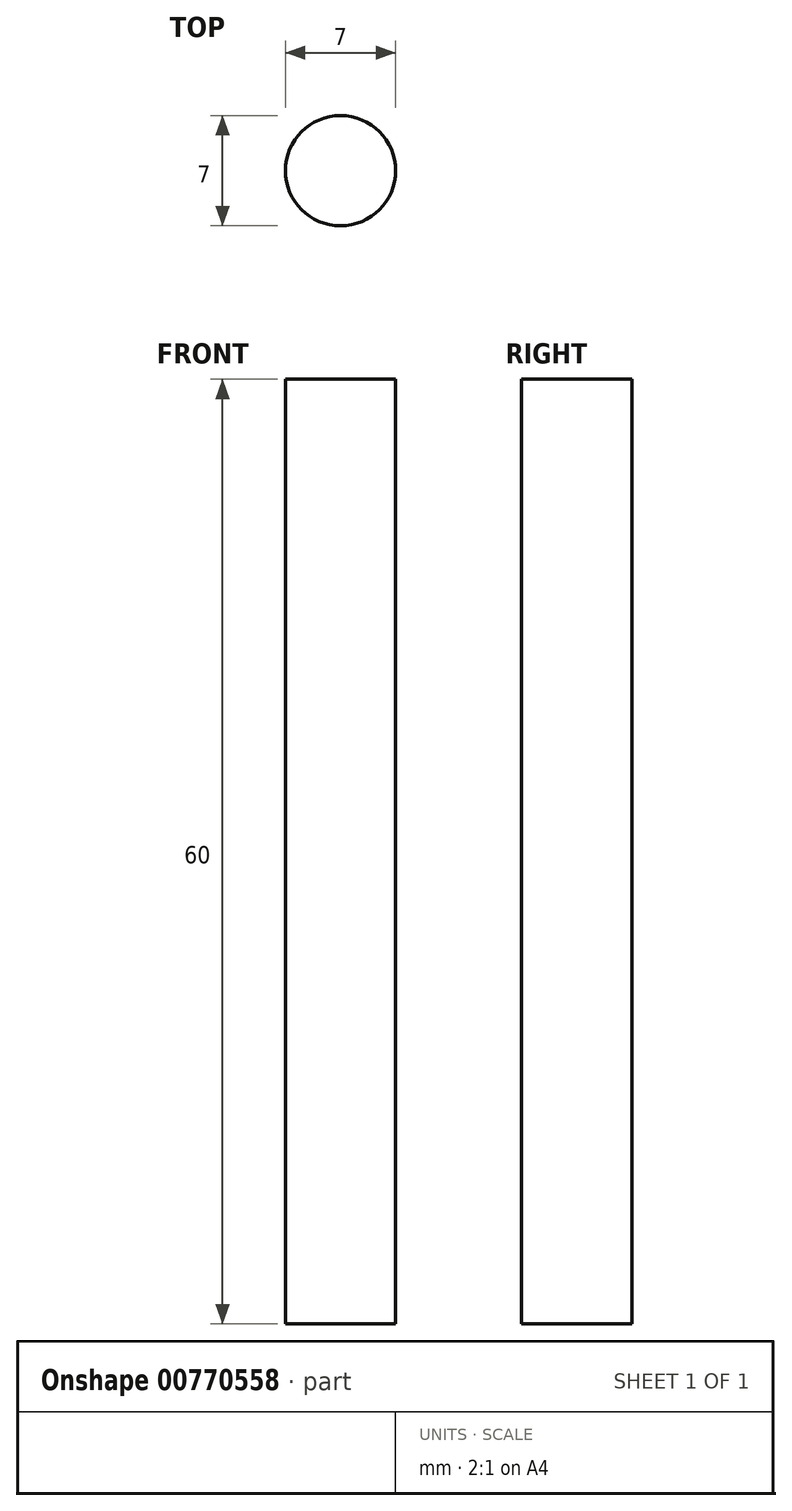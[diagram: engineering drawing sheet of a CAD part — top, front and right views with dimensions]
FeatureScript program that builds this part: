
annotation { "Feature Type Name" : "Feature", "Feature Type Description" : "" }
export const myFeature = defineFeature(function(context is Context, id is Id, definition is map)
    precondition{}
    {
        {
            var Q0;
            Q0=qCreatedBy(makeId("Top.planeOp"),FACE);
            var sketch = newSketch(context, id + "F0", { "sketchPlane" : qUnion([Q0])});
            skCircle(sketch, "E0", {"center": v(0, 0) * mm, "radius": 3.5 * mm});
            skSolve(sketch);
        }
        {
            var Q0;
            Q0 = qSketchRegion(id + "F0", true);
            extrude(context, id + "F1", {"entities" : qUnion([Q0]), "depth" : 60 * mm, "offsetDistance" : 25 * mm});
        }
    });
